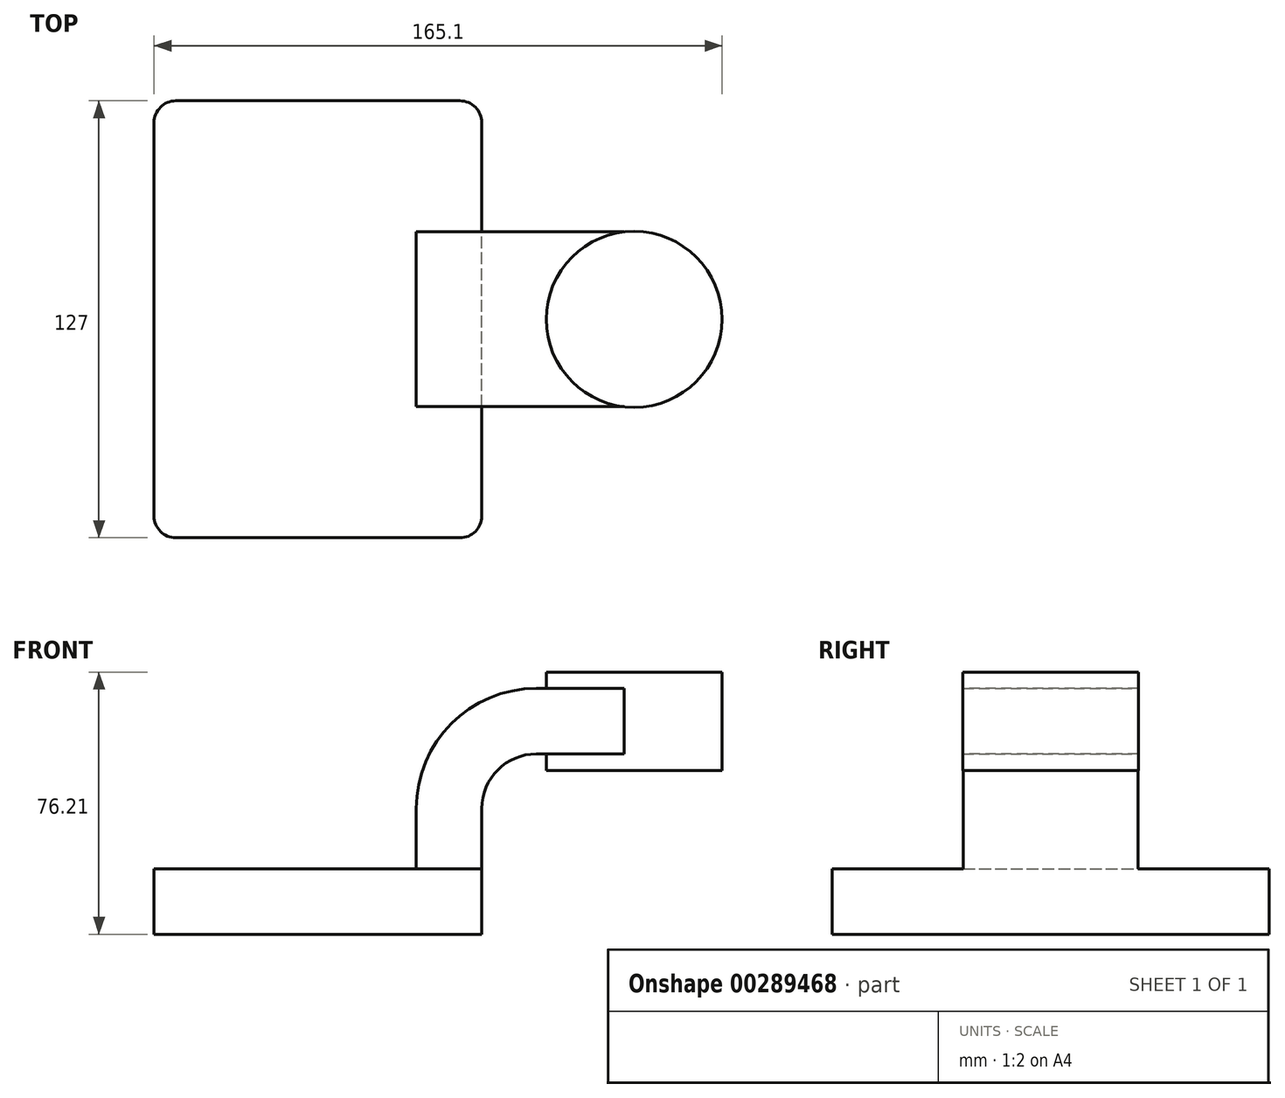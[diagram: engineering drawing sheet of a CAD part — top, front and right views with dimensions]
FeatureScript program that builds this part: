
annotation { "Feature Type Name" : "Feature", "Feature Type Description" : "" }
export const myFeature = defineFeature(function(context is Context, id is Id, definition is map)
    precondition{}
    {
        {
            var Q0;
            Q0=qCreatedBy(makeId("Front.planeOp"),FACE);
            var sketch = newSketch(context, id + "F0", { "sketchPlane" : qUnion([Q0])});
            skLineSegment(sketch, "E0.bottom", {"start": v(47.63, -9.53) * mm, "end": v(-47.63, -9.53) * mm});
            skLineSegment(sketch, "E0.top", {"start": v(47.62, 9.53) * mm, "end": v(-47.63, 9.52) * mm});
            skLineSegment(sketch, "E0.left", {"start": v(47.63, -9.53) * mm, "end": v(47.63, 9.53) * mm});
            skLineSegment(sketch, "E0.right", {"start": v(-47.62, -9.53) * mm, "end": v(-47.63, 9.52) * mm});
            skPoint(sketch, "E0.middle", {"position": v(0, 0) * mm});
            skLineSegment(sketch, "E1", {"start": v(47.62, 9.53) * mm, "end": v(47.62, 27) * mm});
            skArc(sketch, "E2", {"start": v(47.62, 27) * mm, "mid": v(52.27, 38.23) * mm, "end": v(63.5, 42.88) * mm});
            skLineSegment(sketch, "E3", {"start": v(63.5, 42.88) * mm, "end": v(91.91, 42.88) * mm});
            skLineSegment(sketch, "E4.bottom", {"start": v(117.48, 38.1) * mm, "end": v(66.67, 38.1) * mm});
            skLineSegment(sketch, "E4.top", {"start": v(117.48, 66.67) * mm, "end": v(66.67, 66.67) * mm});
            skLineSegment(sketch, "E4.left", {"start": v(117.48, 38.1) * mm, "end": v(117.48, 66.67) * mm});
            skLineSegment(sketch, "E4.right", {"start": v(66.67, 38.1) * mm, "end": v(66.67, 66.67) * mm});
            skPoint(sketch, "E4.middle", {"position": v(92.08, 52.39) * mm});
            skLineSegment(sketch, "E5.0", {"start": v(63.5, 61.93) * mm, "end": v(91.91, 61.93) * mm});
            skArc(sketch, "E5.1", {"start": v(28.58, 27) * mm, "mid": v(38.8, 51.7) * mm, "end": v(63.5, 61.93) * mm});
            skLineSegment(sketch, "E5.2", {"start": v(28.57, 9.53) * mm, "end": v(28.57, 27) * mm});
            skLineSegment(sketch, "E6", {"start": v(91.91, 66.67) * mm, "end": v(91.91, 38.1) * mm});
            skPoint(sketch, "E6.startSnap0", {"position": v(92.08, 66.67) * mm});
            skFitSpline(sketch, "E7", {"points": [v(-47.63, 9.52) * mm, v(63.5, 61.93) * mm], "startDerivative": vector(1.58, 62.75) * mm, "endDerivative": vector(190.5, -0.97) * mm});
            skSolve(sketch);
        }
        {
            var Q0;
            Q0=makeQuery(id+"F0.imprint","IMPRINT",FACE,{"disambiguationData":[TD([[makeQuery(id+"F0.imprint","IMPRINT",EDGE,{"derivedFrom":sQuery(id+"F0.wireOp",EDGE,"E0.bottom")}),-1.0]])]});
            extrude(context, id + "F1", {"entities" : qUnion([Q0]), "endBound" : BoundingType.SYMMETRIC, "depth" : 127 * mm});
        }
        {
            var Q0;
            {var subQ4=sQuery(id+"F0.wireOp",EDGE,"E1");Q0=makeQuery(id+"F0.imprint","IMPRINT",FACE,{"disambiguationData":[TD([[makeQuery(id+"F0.imprint","IMPRINT",EDGE,{"derivedFrom":subQ4}),1.0]])]});}
            extrude(context, id + "F2", {"entities" : qUnion([Q0]), "operationType" : NewBodyOperationType.ADD, "endBound" : BoundingType.SYMMETRIC, "depth" : 50.8 * mm});
        }
        {
            var Q0;
            Q0=makeQuery(id+"F0.imprint","IMPRINT",FACE,{"disambiguationData":[TD([[makeQuery(id+"F0.imprint","IMPRINT",EDGE,{"derivedFrom":sQuery(id+"F0.wireOp",EDGE,"E5.1")}),1.0]])]});
            extrude(context, id + "F3", {"entities" : qUnion([Q0]), "operationType" : NewBodyOperationType.ADD, "endBound" : BoundingType.SYMMETRIC, "depth" : 15.88 * mm});
        }
        {
            var Q0;
            Q0=makeQuery(id+"F2.opExtrude","SWEPT_FACE",FACE,{"disambiguationData":[OSD([sQuery(id+"F0.wireOp",EDGE,"E4.right")])]});
            extrude(context, id + "F4", {"entities" : qUnion([Q0]), "operationType" : NewBodyOperationType.ADD, "depth" : 25.4 * mm});
        }
        {
            var Q0;
            {var subQ0=sQuery(id+"F0.wireOp",EDGE,"E4.left");Q0=makeQuery(id+"F0.imprint","IMPRINT",FACE,{"disambiguationData":[TD([[makeQuery(id+"F0.imprint","IMPRINT",EDGE,{"derivedFrom":subQ0}),1.0]])]});}
            var Q1;
            Q1=sQuery(id+"F0.wireOp",EDGE,"E6");
            revolve(context, id + "F5", {"operationType" : NewBodyOperationType.ADD, "entities" : qUnion([Q0]), "axis" : qUnion([Q1]), "revolveType" : RevolveType.FULL});
        }
        {
            var Q0;
            Q0=makeQuery(id+"F1.opExtrude","CAP_EDGE",EDGE,{"disambiguationData":[OSD([sQuery(id+"F0.wireOp",EDGE,"E0.left")])],"isStart":true});
            var Q1;
            Q1=makeQuery(id+"F1.opExtrude","CAP_EDGE",EDGE,{"disambiguationData":[OSD([sQuery(id+"F0.wireOp",EDGE,"E0.right")])],"isStart":true});
            var Q2;
            Q2=makeQuery(id+"F1.opExtrude","CAP_EDGE",EDGE,{"disambiguationData":[OSD([sQuery(id+"F0.wireOp",EDGE,"E0.right")])],"isStart":false});
            var Q3;
            Q3=makeQuery(id+"F1.opExtrude","CAP_EDGE",EDGE,{"disambiguationData":[OSD([sQuery(id+"F0.wireOp",EDGE,"E0.left")])],"isStart":false});
            fillet(context, id + "F6", {"entities" : qUnion([Q0, Q1, Q2, Q3]), "radius" : 6.35 * mm, "tangentPropagation" : true, "allowEdgeOverflow" : false});
        }
    });
